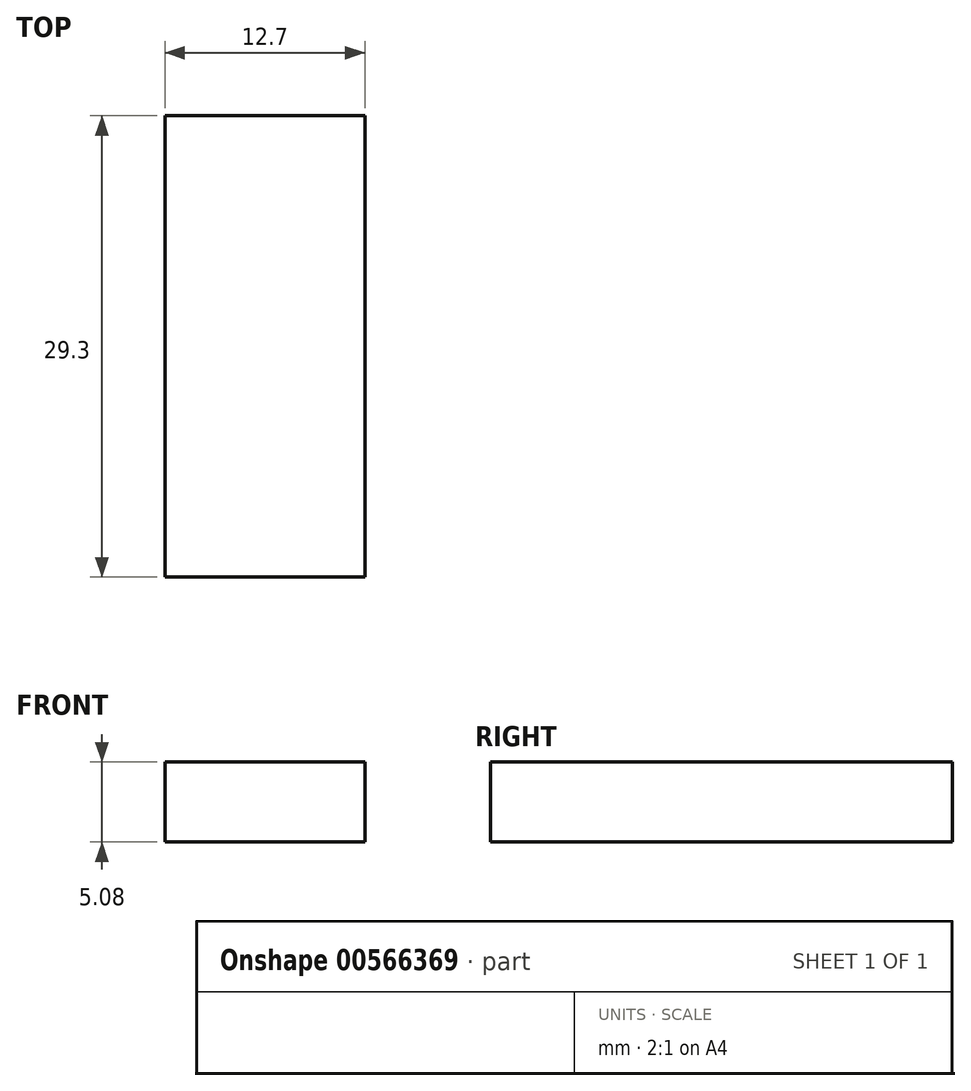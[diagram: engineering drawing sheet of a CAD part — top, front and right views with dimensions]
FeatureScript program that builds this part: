
annotation { "Feature Type Name" : "Feature", "Feature Type Description" : "" }
export const myFeature = defineFeature(function(context is Context, id is Id, definition is map)
    precondition{}
    {
        {
            var Q0;
            Q0=qCreatedBy(makeId("Top.planeOp"),FACE);
            var sketch = newSketch(context, id + "F0", { "sketchPlane" : qUnion([Q0])});
            skLineSegment(sketch, "E0.bottom", {"start": v(6.35, -14.65) * mm, "end": v(-6.35, -14.65) * mm});
            skLineSegment(sketch, "E0.top", {"start": v(6.35, 14.65) * mm, "end": v(-6.35, 14.65) * mm});
            skLineSegment(sketch, "E0.left", {"start": v(6.35, -14.65) * mm, "end": v(6.35, 14.65) * mm});
            skLineSegment(sketch, "E0.right", {"start": v(-6.35, -14.65) * mm, "end": v(-6.35, 14.65) * mm});
            skPoint(sketch, "E0.middle", {"position": v(0, 0) * mm});
            skSolve(sketch);
        }
        {
            var Q0;
            Q0=makeQuery(id+"F0.imprint","IMPRINT",FACE,{"disambiguationData":[TD([[makeQuery(id+"F0.imprint","IMPRINT",EDGE,{"derivedFrom":sQuery(id+"F0.wireOp",EDGE,"E0.bottom")}),-1.0]])]});
            extrude(context, id + "F1", {"entities" : qUnion([Q0]), "depth" : 5.08 * mm, "offsetDistance" : 25.4 * mm});
        }
    });
